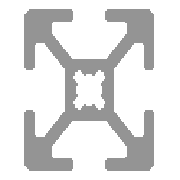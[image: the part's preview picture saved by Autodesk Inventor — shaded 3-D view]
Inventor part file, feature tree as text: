
AUTODESK INVENTOR PART (.ipt)
format: ipt  version: 2017 (Build 210142000, 142)  size: 228,864 bytes
history: native  units: in
note: dims shown in document units (in); Inventor stores cm internally (conversion verified against a paired STEP export)
features: other x3, sketch x1
ambient origin geometry x8: Origin, YZ Plane, XZ Plane, XY Plane, X Axis, Y Axis, Z Axis, Center Point
bodies: Solid1 (feature_tree), Body (feature_tree)
feature tree (4):
  other  "Blocks"
  other  "Start Plane"
  other  "End Plane"
  sketch  "Sketch1"  dims[d2=-0.0in d3=1.0in d4=36.0in d5=0.0in d7=1.0in]
